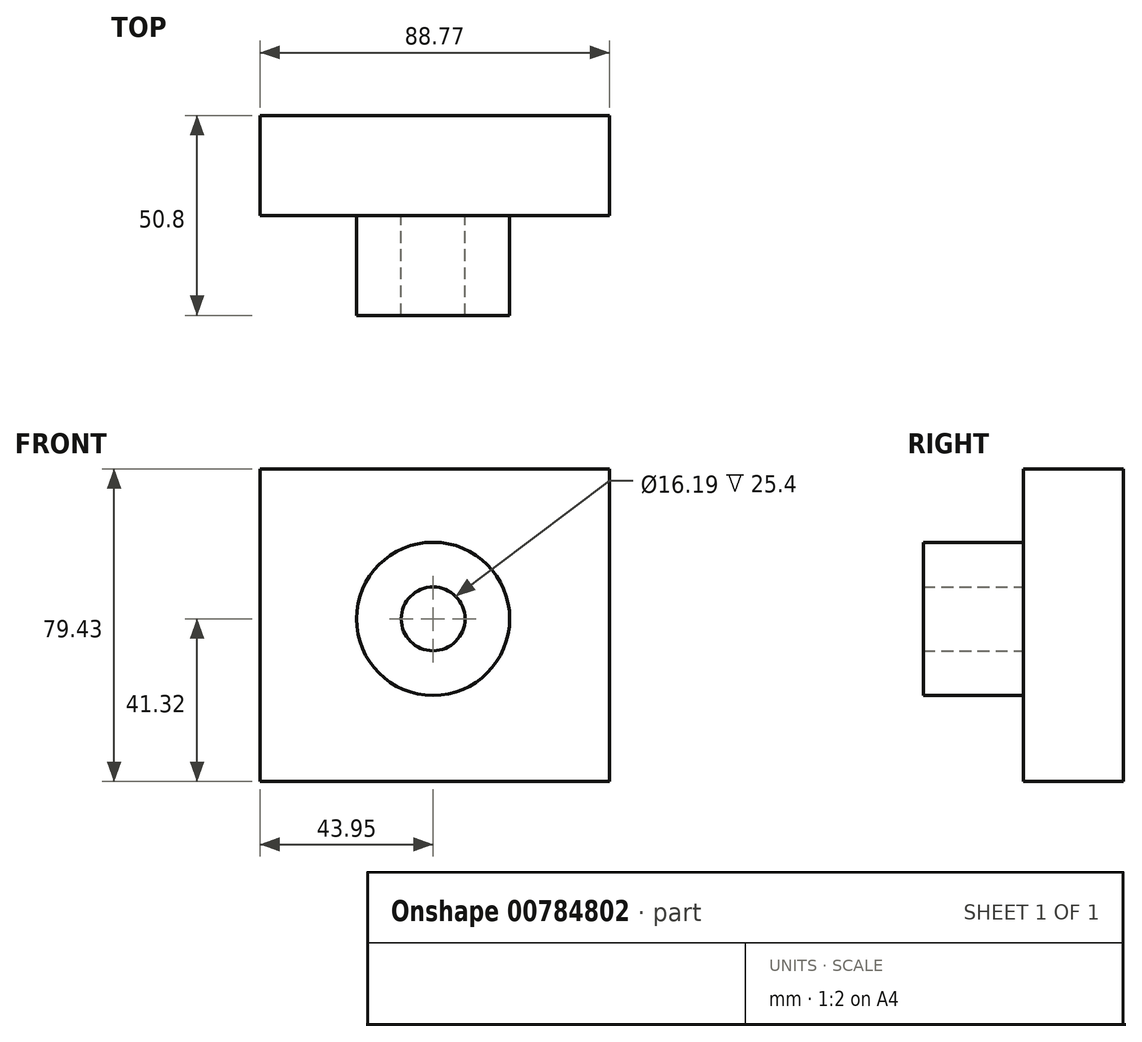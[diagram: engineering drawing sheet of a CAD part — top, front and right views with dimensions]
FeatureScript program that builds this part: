
annotation { "Feature Type Name" : "Feature", "Feature Type Description" : "" }
export const myFeature = defineFeature(function(context is Context, id is Id, definition is map)
    precondition{}
    {
        {
            var Q0;
            Q0=qCreatedBy(makeId("Front.planeOp"),FACE);
            var sketch = newSketch(context, id + "F0", { "sketchPlane" : qUnion([Q0])});
            skLineSegment(sketch, "E0.top", {"start": v(0, 25.4) * mm, "end": v(25.4, 25.4) * mm});
            skLineSegment(sketch, "E0.right", {"start": v(25.4, 0) * mm, "end": v(25.4, 25.4) * mm});
            skLineSegment(sketch, "E1.top", {"start": v(0, 25.4) * mm, "end": v(-25.4, 25.4) * mm});
            skLineSegment(sketch, "E1.right", {"start": v(-25.4, 0) * mm, "end": v(-25.4, 25.4) * mm});
            skLineSegment(sketch, "E2.top", {"start": v(0, -25.4) * mm, "end": v(25.4, -25.4) * mm});
            skLineSegment(sketch, "E2.right", {"start": v(25.4, 0) * mm, "end": v(25.4, -25.4) * mm});
            skLineSegment(sketch, "E3.top", {"start": v(0, -25.4) * mm, "end": v(-25.4, -25.4) * mm});
            skLineSegment(sketch, "E3.right", {"start": v(-25.4, 0) * mm, "end": v(-25.4, -25.4) * mm});
            skCircle(sketch, "E4", {"center": v(0, 0) * mm, "radius": 8.1 * mm});
            skCircle(sketch, "E5", {"center": v(0, 0) * mm, "radius": 14.09 * mm});
            skCircle(sketch, "E6", {"center": v(0, 0) * mm, "radius": 19.46 * mm});
            skSolve(sketch);
        }
        {
            var Q0;
            Q0=makeQuery(id+"F0.imprint","IMPRINT",FACE,{"disambiguationData":[TD([[makeQuery(id+"F0.imprint","IMPRINT",EDGE,{"derivedFrom":sQuery(id+"F0.wireOp",EDGE,"E4")}),-1.0]])]});
            var Q1;
            Q1=makeQuery(id+"F0.imprint","IMPRINT",FACE,{"disambiguationData":[TD([[makeQuery(id+"F0.imprint","IMPRINT",EDGE,{"derivedFrom":sQuery(id+"F0.wireOp",EDGE,"E5")}),-1.0]])]});
            extrude(context, id + "F1", {"entities" : qUnion([Q0, Q1]), "depth" : 50.8 * mm, "offsetDistance" : 25.4 * mm});
        }
        {
            var Q0;
            Q0=qCreatedBy(makeId("Front.planeOp"),FACE);
            var sketch = newSketch(context, id + "F2", { "sketchPlane" : qUnion([Q0])});
            skLineSegment(sketch, "E7.bottom", {"start": v(-43.95, 38.1) * mm, "end": v(44.82, 38.1) * mm});
            skLineSegment(sketch, "E7.top", {"start": v(-43.95, -41.32) * mm, "end": v(44.82, -41.32) * mm});
            skLineSegment(sketch, "E7.left", {"start": v(-43.95, 38.1) * mm, "end": v(-43.95, -41.32) * mm});
            skLineSegment(sketch, "E7.right", {"start": v(44.82, 38.1) * mm, "end": v(44.82, -41.32) * mm});
            skSolve(sketch);
        }
        {
            var Q0;
            Q0=makeQuery(id+"F2.imprint","IMPRINT",FACE,{"disambiguationData":[TD([[makeQuery(id+"F2.imprint","IMPRINT",EDGE,{"derivedFrom":sQuery(id+"F2.wireOp",EDGE,"E7.bottom")}),-1.0]])]});
            extrude(context, id + "F3", {"entities" : qUnion([Q0]), "operationType" : NewBodyOperationType.ADD, "depth" : 25.4 * mm, "offsetDistance" : 25.4 * mm});
        }
    });
